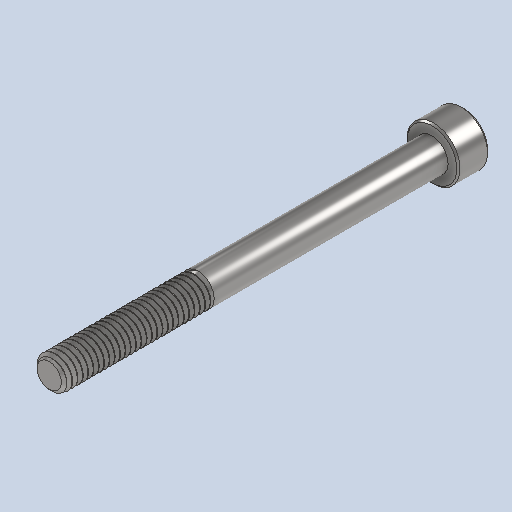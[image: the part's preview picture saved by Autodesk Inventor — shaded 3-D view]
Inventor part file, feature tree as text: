
AUTODESK INVENTOR PART (.ipt)
format: ipt  version: 2024 (Build 280153000, 153)  size: 710,144 bytes
history: native  units: in
note: dims shown in document units (in); Inventor stores cm internally (conversion verified against a paired STEP export)
features: chamfer x1
ambient origin geometry x8: Origin, YZ Plane, XZ Plane, XY Plane, X Axis, Y Axis, Z Axis, Center Point
bodies: Solid1 (feature_tree)
feature tree (1):
  chamfer  "Chamfer2"  [1 undecoded]
note: 1 required parameter value undecoded (feature->parameter linkage not recoverable at this tier; creation-order binding heuristic only, values carry confidence <= 0.55)
